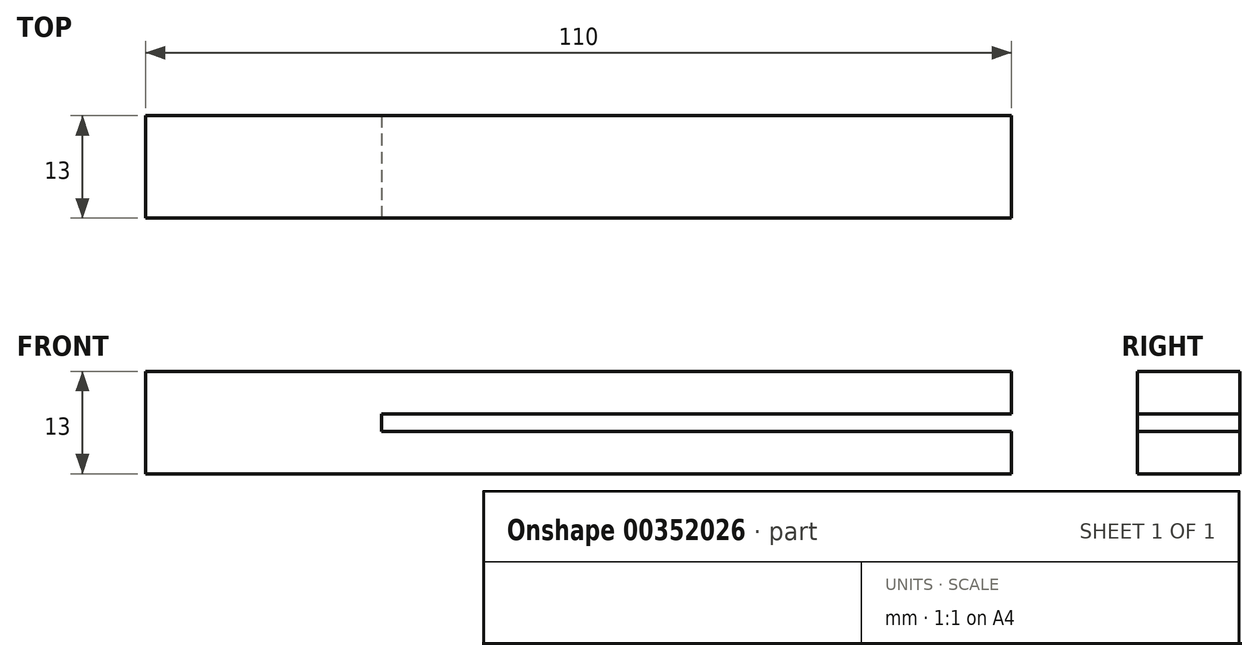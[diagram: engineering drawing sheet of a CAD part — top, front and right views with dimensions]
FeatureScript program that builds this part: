
annotation { "Feature Type Name" : "Feature", "Feature Type Description" : "" }
export const myFeature = defineFeature(function(context is Context, id is Id, definition is map)
    precondition{}
    {
        {
            var Q0;
            Q0=qCreatedBy(makeId("Right.planeOp"),FACE);
            var sketch = newSketch(context, id + "F0", { "sketchPlane" : qUnion([Q0])});
            skLineSegment(sketch, "E0.bottom", {"start": v(-6.5, 6.5) * mm, "end": v(6.5, 6.5) * mm});
            skLineSegment(sketch, "E0.top", {"start": v(-6.5, -6.5) * mm, "end": v(6.5, -6.5) * mm});
            skLineSegment(sketch, "E0.left", {"start": v(-6.5, 6.5) * mm, "end": v(-6.5, -6.5) * mm});
            skLineSegment(sketch, "E0.right", {"start": v(6.5, 6.5) * mm, "end": v(6.5, -6.5) * mm});
            skSolve(sketch);
        }
        {
            var Q0;
            Q0=qSketchRegion(id+"F0",true);
            extrude(context, id + "F1", {"entities" : qUnion([Q0]), "depth" : 110 * mm});
        }
        {
            var Q0;
            Q0=qCreatedBy(makeId("Right.planeOp"),FACE);
            cPlane(context, id + "F2", {"entities" : qUnion([Q0]), "cplaneType" : CPlaneType.OFFSET, "offset" : 110 * mm, "width" : 150 * mm, "height" : 150 * mm});
        }
        {
            var Q0;
            Q0=qCreatedBy(id+"F2.planeOp",FACE);
            var sketch = newSketch(context, id + "F3", { "sketchPlane" : qUnion([Q0])});
            skLineSegment(sketch, "E1", {"start": v(-6.5, 1.1) * mm, "end": v(-6.5, -1.1) * mm});
            skLineSegment(sketch, "E2", {"start": v(-6.5, -1.1) * mm, "end": v(6.5, -1.1) * mm});
            skLineSegment(sketch, "E3", {"start": v(6.5, -1.1) * mm, "end": v(6.5, 1.1) * mm});
            skLineSegment(sketch, "E4", {"start": v(6.5, 1.1) * mm, "end": v(-6.5, 1.1) * mm});
            skSolve(sketch);
        }
        {
            var Q0;
            Q0=makeQuery(id+"F3.imprint","IMPRINT",FACE,{"disambiguationData":[TD([[makeQuery(id+"F3.imprint","IMPRINT",EDGE,{"derivedFrom":sQuery(id+"F3.wireOp",EDGE,"E1")}),1.0]])]});
            extrude(context, id + "F4", {"entities" : qUnion([Q0]), "operationType" : NewBodyOperationType.REMOVE, "oppositeDirection" : true, "depth" : 80 * mm});
        }
    });
